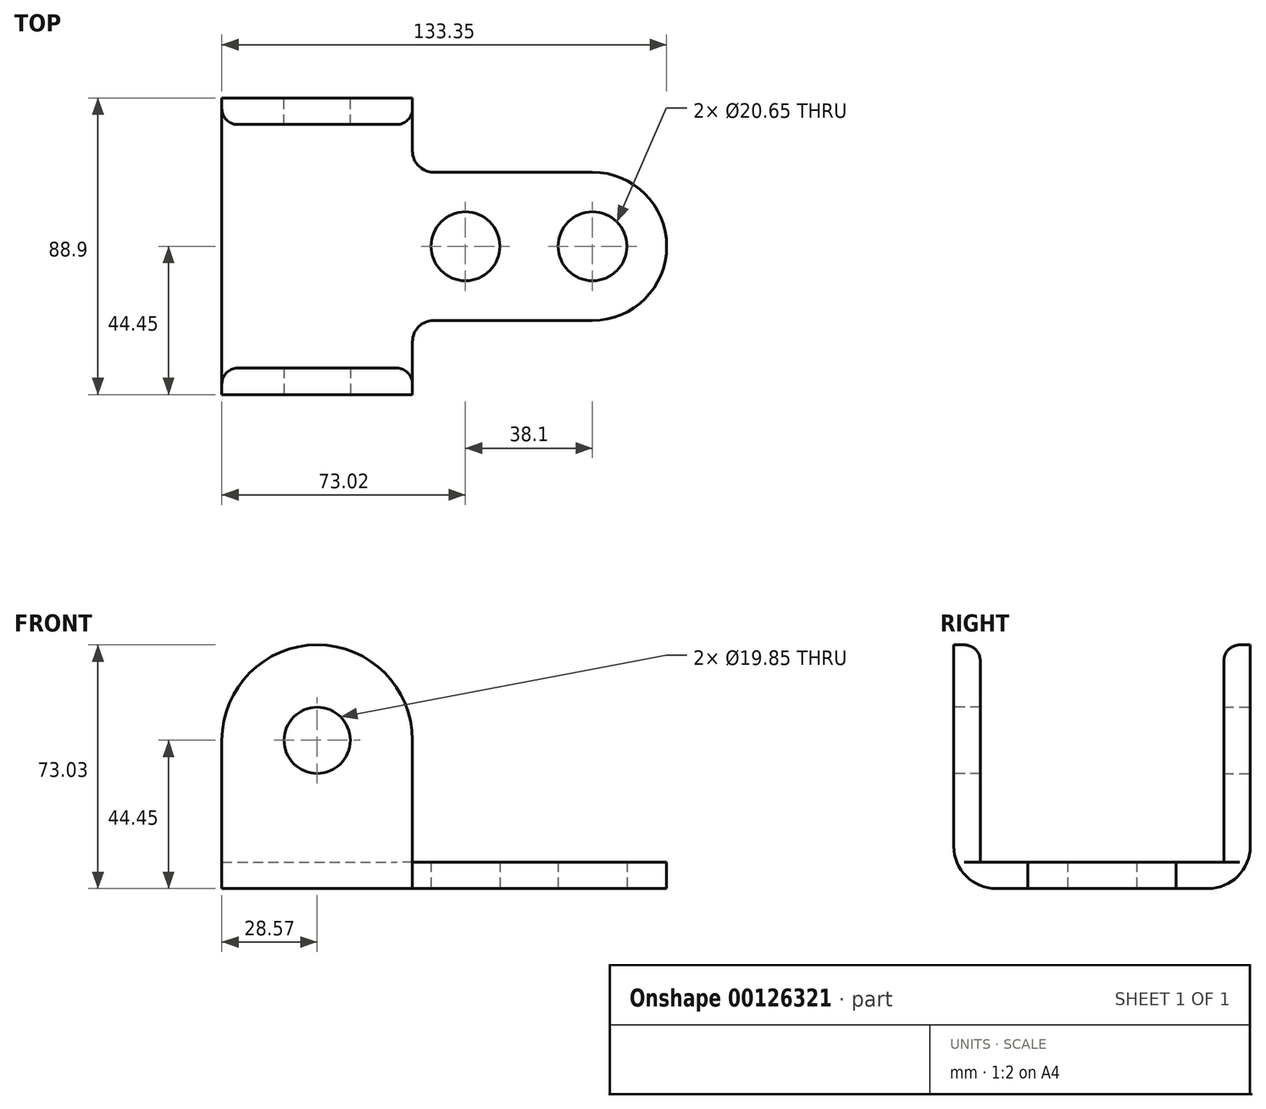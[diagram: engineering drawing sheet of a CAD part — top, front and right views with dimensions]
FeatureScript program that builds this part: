
annotation { "Feature Type Name" : "Feature", "Feature Type Description" : "" }
export const myFeature = defineFeature(function(context is Context, id is Id, definition is map)
    precondition{}
    {
        {
            var Q0;
            Q0=qCreatedBy(makeId("Top.planeOp"),FACE);
            var sketch = newSketch(context, id + "F0", { "sketchPlane" : qUnion([Q0])});
            skCircle(sketch, "E0", {"center": v(0, 0) * mm, "radius": 10.33 * mm});
            skCircle(sketch, "E1", {"center": v(-38.1, 0) * mm, "radius": 10.33 * mm});
            skArc(sketch, "E2", {"start": v(0, -22.23) * mm, "mid": v(22.23, 0) * mm, "end": v(0, 22.23) * mm});
            skLineSegment(sketch, "E3.left", {"start": v(-111.12, 44.45) * mm, "end": v(-111.12, -44.45) * mm});
            skLineSegment(sketch, "E4", {"start": v(0, 22.23) * mm, "end": v(-53.98, 22.23) * mm});
            skLineSegment(sketch, "E5", {"start": v(0, -22.23) * mm, "end": v(-53.97, -22.23) * mm});
            skLineSegment(sketch, "E6", {"start": v(-111.12, 44.45) * mm, "end": v(-53.98, 44.45) * mm});
            skLineSegment(sketch, "E7", {"start": v(-53.98, 44.45) * mm, "end": v(-53.98, 22.23) * mm});
            skLineSegment(sketch, "E8", {"start": v(-111.12, -44.45) * mm, "end": v(-53.97, -44.45) * mm});
            skLineSegment(sketch, "E9", {"start": v(-111.12, 0) * mm, "end": v(41.67, 0) * mm, "construction": true});
            skLineSegment(sketch, "E10", {"start": v(-53.97, -44.45) * mm, "end": v(-53.97, -22.23) * mm});
            skPoint(sketch, "E11.end.orphan", {"position": v(-53.97, -22.23) * mm});
            skSolve(sketch);
        }
        {
            var Q0;
            Q0 = qSketchRegion(id + "F0", true);
            extrude(context, id + "F1", {"entities" : qUnion([Q0]), "depth" : 7.94 * mm});
        }
        {
            var Q0;
            Q0=makeQuery(id+"F1.opExtrude","SWEPT_EDGE",EDGE,{"disambiguationData":[OSD([sQuery(id+"F0.wireOp",EDGE,"E5"),sQuery(id+"F0.wireOp",EDGE,"E10")])]});
            var Q1;
            Q1=makeQuery(id+"F1.opExtrude","SWEPT_EDGE",EDGE,{"disambiguationData":[OSD([sQuery(id+"F0.wireOp",EDGE,"E4"),sQuery(id+"F0.wireOp",EDGE,"E7")])]});
            fillet(context, id + "F2", {"entities" : qUnion([Q0, Q1]), "radius" : 6.35 * mm, "tangentPropagation" : true, "allowEdgeOverflow" : false});
        }
        {
            var Q0;
            Q0=makeQuery(id+"F1.opExtrude","SWEPT_FACE",FACE,{"disambiguationData":[OSD([sQuery(id+"F0.wireOp",EDGE,"E8")])]});
            var sketch = newSketch(context, id + "F3", { "sketchPlane" : qUnion([Q0])});
            skLineSegment(sketch, "E12.bottom", {"start": v(-111.12, 0) * mm, "end": v(-53.97, 0) * mm});
            skCircle(sketch, "E13", {"center": v(-82.55, 44.45) * mm, "radius": 9.92 * mm});
            skLineSegment(sketch, "E14", {"start": v(-82.55, 73.03) * mm, "end": v(-82.55, 0) * mm, "construction": true});
            skLineSegment(sketch, "E15", {"start": v(-111.12, 0) * mm, "end": v(-111.12, 44.45) * mm});
            skLineSegment(sketch, "E16", {"start": v(-53.97, 44.45) * mm, "end": v(-53.97, 0) * mm});
            skArc(sketch, "E17", {"start": v(-53.97, 44.45) * mm, "mid": v(-82.55, 73.03) * mm, "end": v(-111.12, 44.45) * mm});
            skPoint(sketch, "E18", {"position": v(-111.12, 0) * mm});
            skSolve(sketch);
        }
        {
            var Q0;
            Q0=makeQuery(id+"F3.imprint","IMPRINT",FACE,{"disambiguationData":[TD([[makeQuery(id+"F3.imprint","IMPRINT",EDGE,{"derivedFrom":sQuery(id+"F3.wireOp",EDGE,"E13")}),-1.0]])]});
            extrude(context, id + "F4", {"entities" : qUnion([Q0]), "operationType" : NewBodyOperationType.ADD, "oppositeDirection" : true, "depth" : 7.94 * mm});
        }
        {
            var Q0;
            Q0=makeQuery(id+"F1.opExtrude","SWEPT_BODY",BODY,{"disambiguationData":[OSD([sQuery(id+"F0.wireOp",EDGE,"E0"),sQuery(id+"F0.wireOp",EDGE,"E1"),sQuery(id+"F0.wireOp",EDGE,"E2"),sQuery(id+"F0.wireOp",EDGE,"E3.left"),sQuery(id+"F0.wireOp",EDGE,"E4"),sQuery(id+"F0.wireOp",EDGE,"E5"),sQuery(id+"F0.wireOp",EDGE,"E6"),sQuery(id+"F0.wireOp",EDGE,"E7"),sQuery(id+"F0.wireOp",EDGE,"E8"),sQuery(id+"F0.wireOp",EDGE,"E10")])]});
            var Q1;
            Q1=qCreatedBy(makeId("Front.planeOp"),FACE);
            mirror(context, id + "F5", {"operationType" : NewBodyOperationType.ADD, "entities" : qUnion([Q0]), "mirrorPlane" : qUnion([Q1])});
        }
        {
            var Q0;
            Q0=makeQuery(id+"F1.opExtrude","CAP_EDGE",EDGE,{"disambiguationData":[OSD([sQuery(id+"F0.wireOp",EDGE,"E6")])],"isStart":true});
            var Q1;
            Q1=makeQuery(id+"F1.opExtrude","CAP_EDGE",EDGE,{"disambiguationData":[OSD([sQuery(id+"F0.wireOp",EDGE,"E8")])],"isStart":true});
            fillet(context, id + "F6", {"entities" : qUnion([Q0, Q1]), "radius" : 12.7 * mm, "tangentPropagation" : true, "allowEdgeOverflow" : false});
        }
        {
            var Q0;
            Q0=makeQuery(id+"F5.opPattern","COPY",EDGE,{"derivedFrom":makeQuery(id+"F4.opExtrude","CAP_EDGE",EDGE,{"disambiguationData":[OSD([sQuery(id+"F3.wireOp",EDGE,"E17")])],"isStart":false}),"instanceName":"1"});
            var Q1;
            Q1=makeQuery(id+"F4.opExtrude","CAP_EDGE",EDGE,{"disambiguationData":[OSD([sQuery(id+"F3.wireOp",EDGE,"E17")])],"isStart":false});
            fillet(context, id + "F7", {"entities" : qUnion([Q0, Q1]), "radius" : 4.76 * mm, "tangentPropagation" : true, "allowEdgeOverflow" : false});
        }
    });
